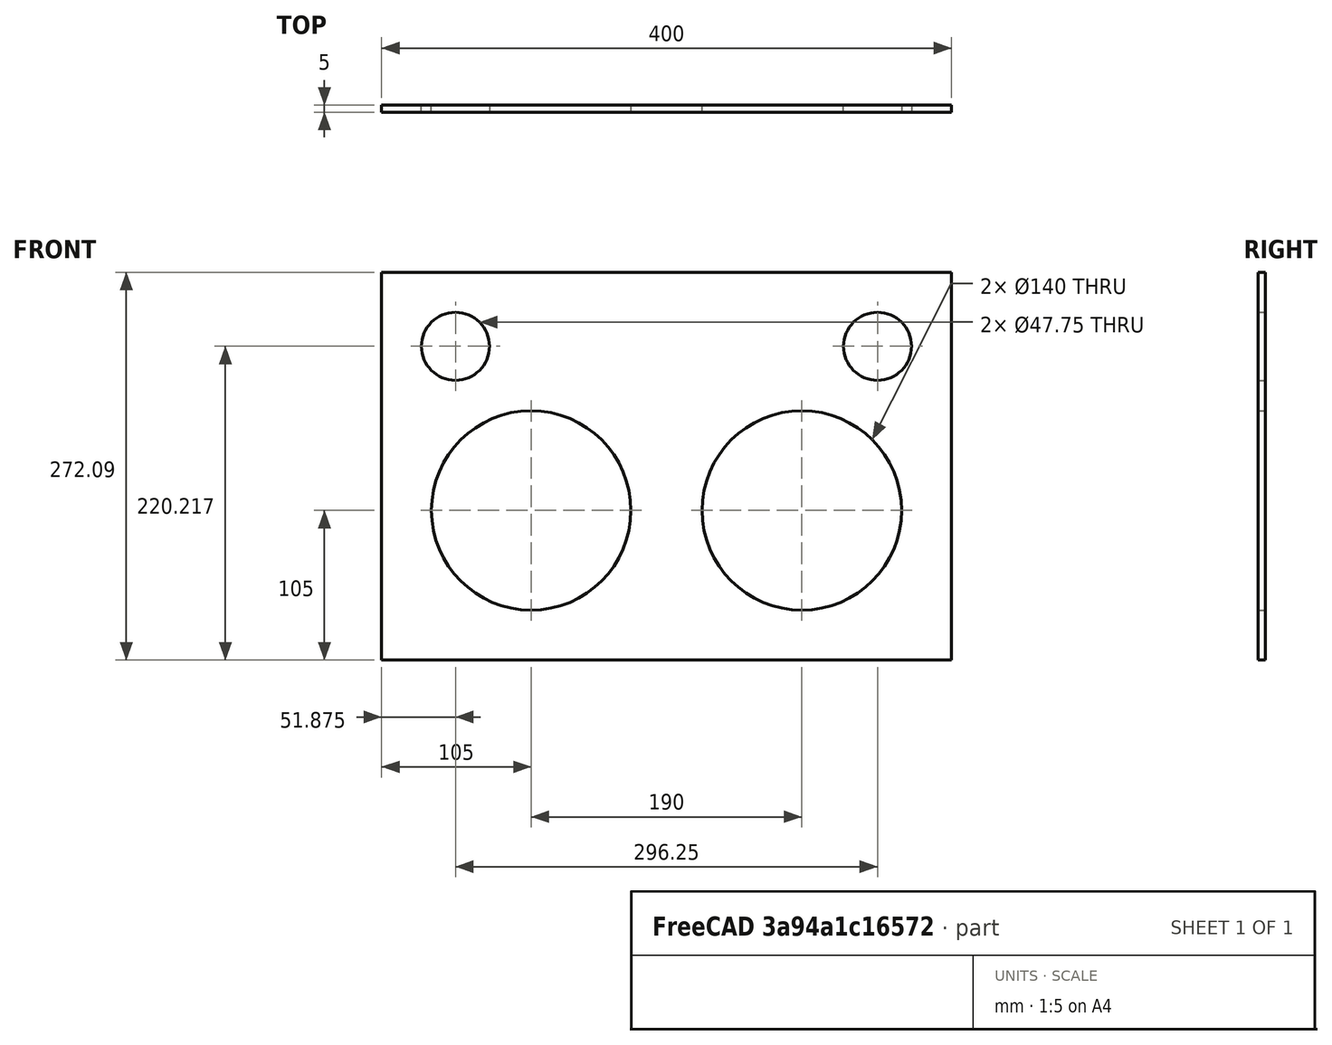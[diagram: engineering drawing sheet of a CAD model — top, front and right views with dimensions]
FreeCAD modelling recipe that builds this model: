
FCSTD DOCUMENT  (FreeCAD 0.22R38622 (Git))
Label: Final design
License: All rights reserved
LicenseURL: https://en.wikipedia.org/wiki/All_rights_reserved
objects: Sketcher::SketchObject×1, PartDesign::Pad×1, PartDesign::Body×1
note: 6 computed .brp shape members not serialized (recipe doc carries the construction recipe); baked Part::Feature solids carry a one-line shape summary decoded from their .brp

FEATURE [Sketcher::SketchObject] Sketch
  ArcFitTolerance = 1e-06
  AttachmentSupport = -> [XZ_Plane]
  FullyConstrained = true
  MakeInternals = false
  MapMode = 5
  Placement = pos=(0,0,0) rot=(1,0,0;1.5708rad)
  sketch-geometry (12):
    g0: Circle [constr] CenterX=95 CenterY=0 CenterZ=0 NormalX=0 NormalY=0 NormalZ=1 AngleXU=0 Radius=85
    g1: Circle [constr] CenterX=148.125 CenterY=115.217 CenterZ=0 NormalX=0 NormalY=0 NormalZ=1 AngleXU=0 Radius=31.875
    g2: LineSegment StartX=-200 StartY=-105 StartZ=0 EndX=200 EndY=-105 EndZ=0
    g3: LineSegment StartX=200 StartY=-105 StartZ=0 EndX=200 EndY=167.092 EndZ=0
    g4: LineSegment StartX=200 StartY=167.092 StartZ=0 EndX=-200 EndY=167.092 EndZ=0
    g5: LineSegment StartX=-200 StartY=167.092 StartZ=0 EndX=-200 EndY=-105 EndZ=0
    g6: Circle [constr] CenterX=-95 CenterY=0 CenterZ=0 NormalX=0 NormalY=0 NormalZ=1 AngleXU=0 Radius=85
    g7: Circle [constr] CenterX=-148.125 CenterY=115.217 CenterZ=0 NormalX=0 NormalY=0 NormalZ=1 AngleXU=0 Radius=31.875
    g8: Circle CenterX=-95 CenterY=0 CenterZ=0 NormalX=0 NormalY=0 NormalZ=1 AngleXU=0 Radius=70
    g9: Circle CenterX=95 CenterY=0 CenterZ=0 NormalX=0 NormalY=0 NormalZ=1 AngleXU=0 Radius=70
    g10: Circle CenterX=-148.125 CenterY=115.217 CenterZ=0 NormalX=0 NormalY=0 NormalZ=1 AngleXU=0 Radius=23.875
    g11: Circle CenterX=148.125 CenterY=115.217 CenterZ=0 NormalX=0 NormalY=0 NormalZ=1 AngleXU=0 Radius=23.875
  constraints (34):
    c: PointOnObject(g0,g-1)
    c: Diameter(g0) = 170
    c: Diameter(g1) = 63.75
    c: Distance(g1,g0) = 10
    c: Coincident(g2,g3)
    c: Coincident(g3,g4)
    c: Coincident(g4,g5)
    c: Coincident(g5,g2)
    c: Horizontal(g2)
    c: Horizontal(g4)
    c: Vertical(g3)
    c: Vertical(g5)
    c: Distance(g1,g4) = 20
    c: Distance(g1,g3) = 20
    c: Distance(g0,g2) = 20
    c: DistanceY(g3,g3) = 272.092
    c: Diameter(g6) = 170
    c: Diameter(g7) = 63.75
    c: Distance(g7,g6) = 10
    c: Distance(g7,g4) = 20
    c: Distance(g7,g5) = 20
    c: DistanceX(g4,g4) = 400
    c: Symmetric(g6,g0,g-2)
    c: Distance(g0,g6) = 20
    c: Distance(g0,g3) = 20
    c: Coincident(g8,g6)
    c: Coincident(g9,g0)
    c: Distance(g6,g8) = 15
    c: Distance(g9,g0) = 15
    c: Coincident(g10,g7)
    c: Coincident(g11,g1)
    c: Distance(g11,g1) = 8
    c: Distance(g10,g7) = 8
    c: Diameter(g11) = 47.75
FEATURE [PartDesign::Pad] Pad
  Direction = (0,-1,2e-16)
  Length = 5
  Length2 = 10
  Placement = pos=(0,0,0) rot=(1,0,0;1.5708rad)
  Profile = -> Sketch
  ReferenceAxis = -> Sketch [N_Axis]
  Refine = true
  Suppressed = false
  Type = 0
FEATURE [PartDesign::Body] Body
  AllowCompound = false
  Group = -> [Sketch,Pad]
  Origin = -> Origin
  Tip = -> Pad
